# Revit family: Crawford LH6080L Load house HM
name_source: partatom
category: Specialty Equipment
revit_build: Autodesk Revit 2015 (Build: 20140606_1530(x64)
units: mm (PartAtom-declared; Revit-internal decimal feet)

## types (1)
- Multi 3300 SMP NW 3200 DH 950
    Angle = 4.00°
    B1 = 750 mm  [stored 2.46063 ft]
    BIMobject category = Loadhouses
    Brand url = http://www.assaabloyentrance.com
    Cladding Material = Stainless Steel AISI 304
    DH = 950 mm  [stored 3.1168 ft]
    Depth = 0
    Design country = Sweden
    Edition number = 1
    GL = 210 mm  [stored 0.688976 ft]
    Horizontal Grid Distance = 500 mm  [stored 1.64042 ft]
    IFC Classification = Door
    Installation instructions = http://www.assaabloyentrance.co.uk
    LF2 = 580 mm  [stored 1.90289 ft]
    Leveller Material = Iron
    Manufacturer country = Sweden
    Manufacturer name = ASSA ABLOY Entrance Systems
    NB = 3200 mm  [stored 10.4987 ft]
    NBS Reference Code = 25-30-20-45
    NBS Reference Description = Loading Bay Systems
    NW = 3300 mm  [stored 10.8268 ft]
    Nominal height = 0 mm  [stored 0 ft]
    Nominal width = 0 mm  [stored 0 ft]
    OL = 350 mm  [stored 1.14829 ft]
    Panels Material = Black PVC Fabric
    Product Guid = 78d41575-4ce3-409a-ac1f-5fa8f4b546f8
    Product SKU = cra_6080_l
    Product certification = http://www.assaabloyentrance.co.uk
    Product data url = https://bimobject.com
    Product family = Docking
    Product group = Loadhouse
    Product url = http://www.assaabloyentrance.co.uk
    QR code = http://bimobject.com
    SME = 1 mm  [stored 0.00328084 ft]
    SME Calc = Yes
    Shelter Material = Fabric Gray
    Supports Material = Aluminum, Anodized Silver
    TB = 3000 mm  [stored 9.84252 ft]
    Technical description = http://www.assaabloyentrance.co.uk
    UNSPSC Code = 39121101
    Uniclass 1.4 Code = L21248
    Uniclass 1.4 Description = Loading bay equipment
    Uniclass 2.0 Code = SS-25-30-20-45
    Uniclass 2.0 Description = Loading Bay Systems
    Youtube clip = https://www.youtube.com

note: [stored X ft] marks values corroborated as IEEE doubles in the binary element streams (Revit-internal decimal feet)

## geometry (parser evidence)
native form markers: Blend x8, Sweep x12
no freeform markers — native parametric forms only
